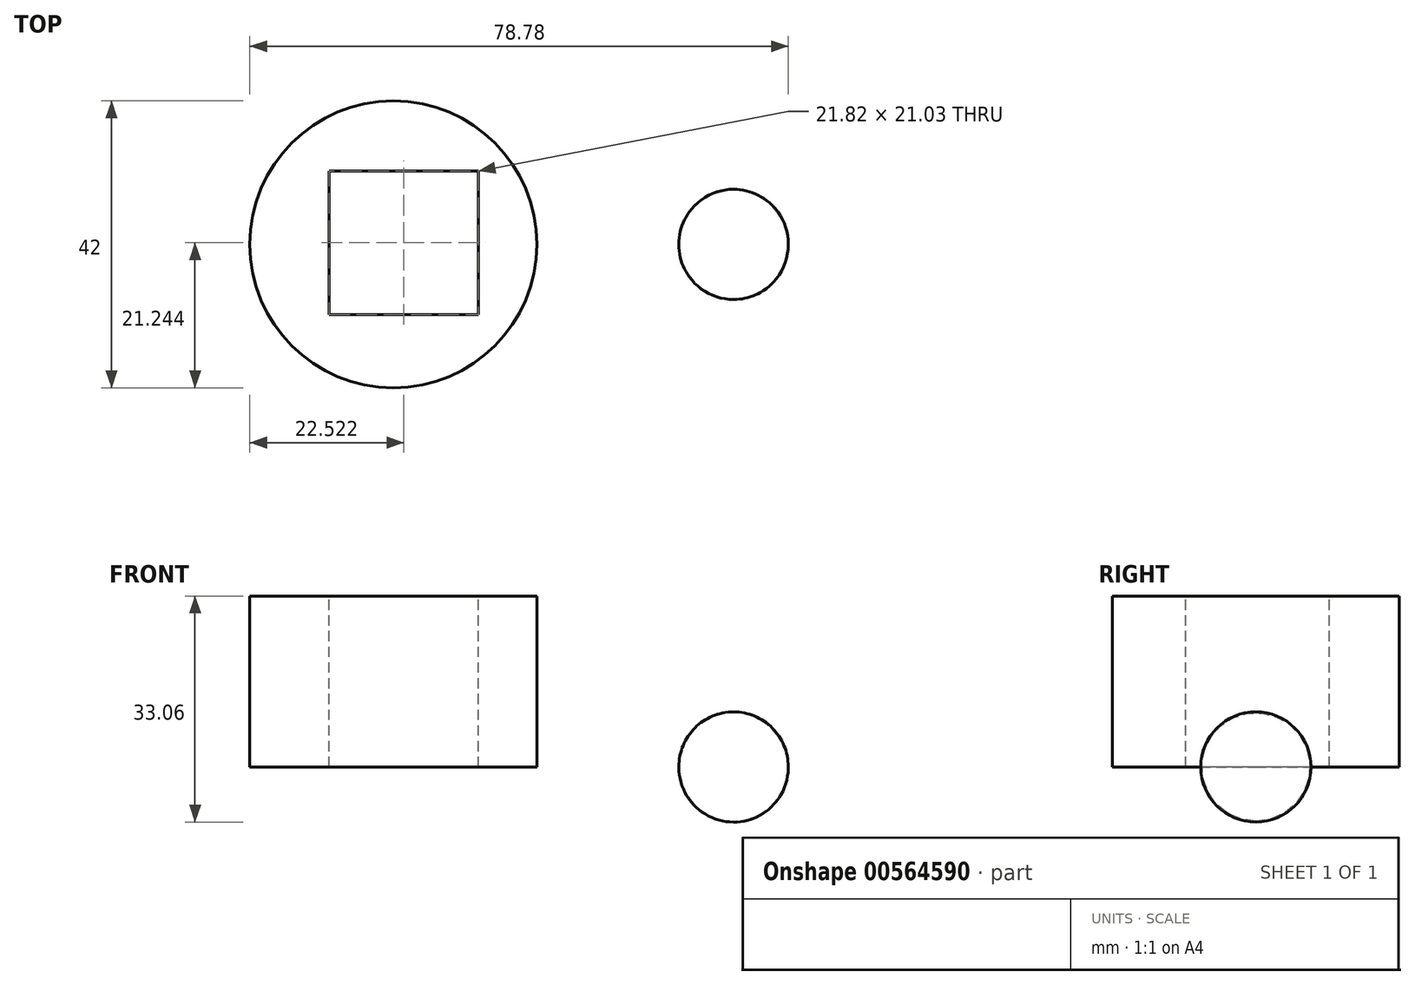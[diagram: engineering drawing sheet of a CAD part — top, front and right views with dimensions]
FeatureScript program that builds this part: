
annotation { "Feature Type Name" : "Feature", "Feature Type Description" : "" }
export const myFeature = defineFeature(function(context is Context, id is Id, definition is map)
    precondition{}
    {
        {
            var Q0;
            Q0=qCreatedBy(makeId("Top.planeOp"),FACE);
            var sketch = newSketch(context, id + "F0", { "sketchPlane" : qUnion([Q0])});
            skCircle(sketch, "E0", {"center": v(0, 0) * mm, "radius": 21 * mm});
            skSolve(sketch);
        }
        {
            var Q0;
            Q0=makeQuery(id+"F0.imprint","IMPRINT",FACE,{"disambiguationData":[TD([[makeQuery(id+"F0.imprint","IMPRINT",EDGE,{"derivedFrom":sQuery(id+"F0.wireOp",EDGE,"E0")}),1.0]])]});
            extrude(context, id + "F1", {"entities" : qUnion([Q0]), "depth" : 25 * mm, "offsetDistance" : 25 * mm});
        }
        {
            var Q0;
            Q0=makeQuery(id+"F1.opExtrude","CAP_FACE",FACE,{"disambiguationData":[OSD([sQuery(id+"F0.wireOp",EDGE,"E0")])],"isStart":false});
            var sketch = newSketch(context, id + "F2", { "sketchPlane" : qUnion([Q0])});
            skLineSegment(sketch, "E1.bottom", {"start": v(-9.39, 10.76) * mm, "end": v(12.43, 10.76) * mm});
            skLineSegment(sketch, "E1.top", {"start": v(-9.39, -10.27) * mm, "end": v(12.43, -10.27) * mm});
            skLineSegment(sketch, "E1.left", {"start": v(-9.39, 10.76) * mm, "end": v(-9.39, -10.27) * mm});
            skLineSegment(sketch, "E1.right", {"start": v(12.43, 10.76) * mm, "end": v(12.43, -10.27) * mm});
            skSolve(sketch);
        }
        {
            var Q0;
            Q0=makeQuery(id+"F2.imprint","IMPRINT",FACE,{"disambiguationData":[TD([[makeQuery(id+"F2.imprint","IMPRINT",EDGE,{"derivedFrom":sQuery(id+"F2.wireOp",EDGE,"E1.bottom")}),-1.0]])]});
            extrude(context, id + "F3", {"entities" : qUnion([Q0]), "operationType" : NewBodyOperationType.REMOVE, "oppositeDirection" : true, "depth" : 30 * mm, "offsetDistance" : 25 * mm});
        }
        {
            var Q0;
            Q0=qCreatedBy(makeId("Top.planeOp"),FACE);
            var sketch = newSketch(context, id + "F4", { "sketchPlane" : qUnion([Q0])});
            skArc(sketch, "E2", {"start": v(57.78, 0) * mm, "mid": v(49.78, 7.94) * mm, "end": v(41.78, 0) * mm});
            skLineSegment(sketch, "E3", {"start": v(41.78, 0) * mm, "end": v(57.78, 0) * mm});
            skSolve(sketch);
        }
        {
            var Q0;
            Q0=makeQuery(id+"F4.imprint","IMPRINT",FACE,{"disambiguationData":[TD([[makeQuery(id+"F4.imprint","IMPRINT",EDGE,{"derivedFrom":sQuery(id+"F4.wireOp",EDGE,"E2")}),1.0]])]});
            var Q1;
            Q1=sQuery(id+"F4.wireOp",EDGE,"E3");
            revolve(context, id + "F5", {"surfaceOperationType" : NewSurfaceOperationType.NEW, "entities" : qUnion([Q0]), "axis" : qUnion([Q1]), "revolveType" : RevolveType.FULL});
        }
    });
